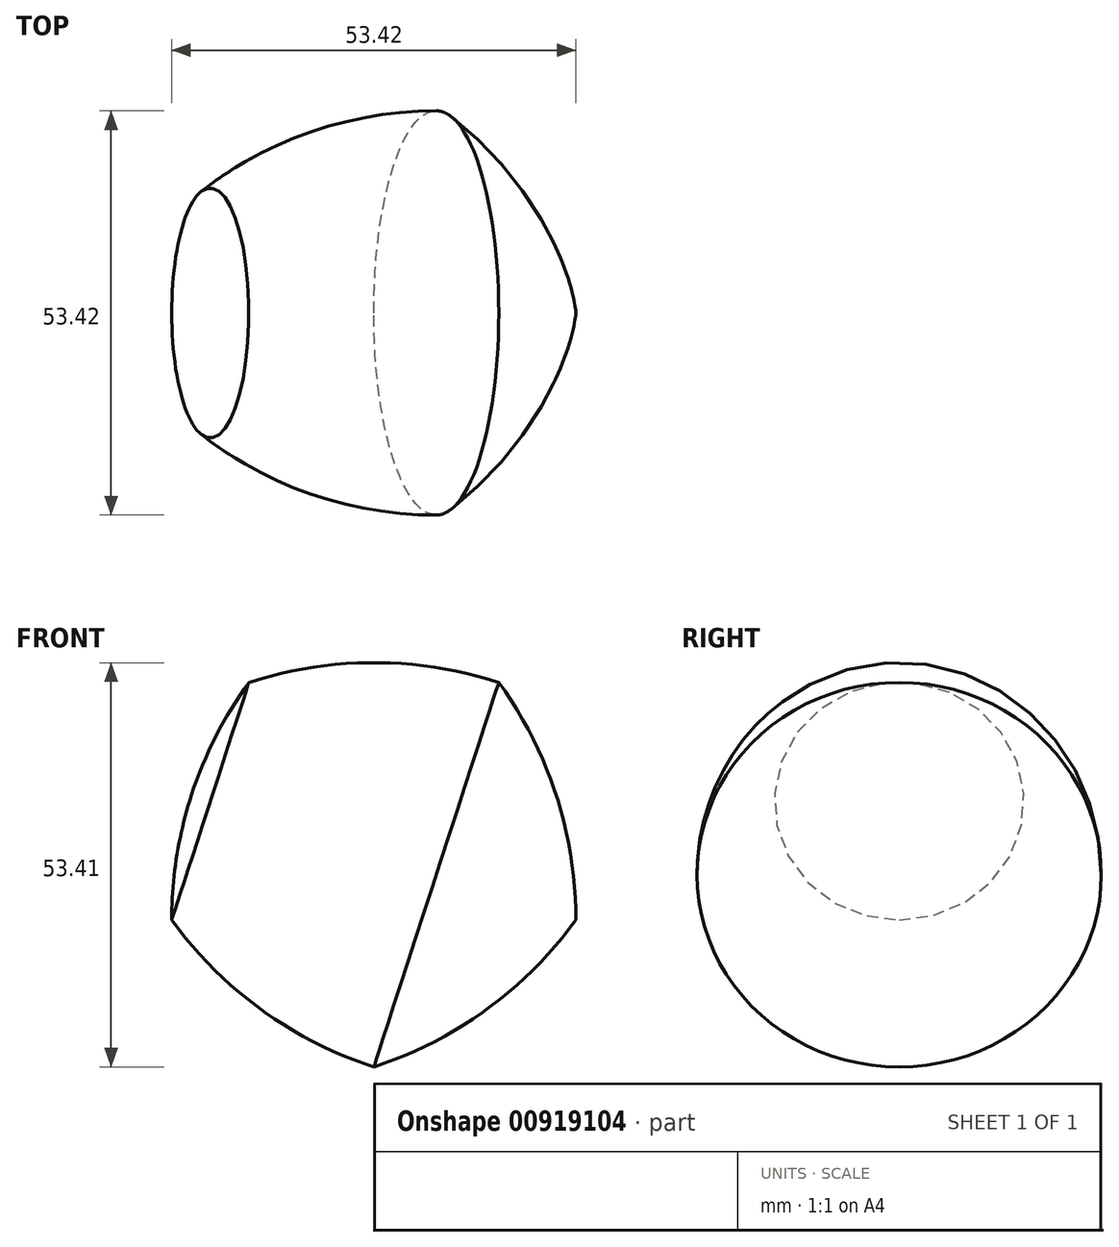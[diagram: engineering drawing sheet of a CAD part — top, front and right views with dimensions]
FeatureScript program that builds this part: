
annotation { "Feature Type Name" : "Feature", "Feature Type Description" : "" }
export const myFeature = defineFeature(function(context is Context, id is Id, definition is map)
    precondition{}
    {
        {
            var Q0;
            Q0=qCreatedBy(makeId("Front.planeOp"),FACE);
            var sketch = newSketch(context, id + "F0", { "sketchPlane" : qUnion([Q0])});
            skCircle(sketch, "E0.cCircle", {"center": v(0, 0) * mm, "radius": 22.72 * mm, "construction": true});
            skLineSegment(sketch, "E0.0", {"start": v(-16.5, 22.72) * mm, "end": v(16.5, 22.72) * mm});
            skLineSegment(sketch, "E0.1", {"start": v(16.5, 22.72) * mm, "end": v(26.7, -8.68) * mm});
            skLineSegment(sketch, "E0.2", {"start": v(26.7, -8.68) * mm, "end": v(0, -28.08) * mm});
            skLineSegment(sketch, "E0.3", {"start": v(0, -28.08) * mm, "end": v(-26.7, -8.68) * mm});
            skLineSegment(sketch, "E0.4", {"start": v(-26.7, -8.68) * mm, "end": v(-16.5, 22.72) * mm});
            skPoint(sketch, "E0.0.midPoint", {"position": v(0, 22.72) * mm});
            skPoint(sketch, "E1", {"position": v(-13.35, -18.38) * mm});
            skLineSegment(sketch, "E2", {"start": v(0, -28.08) * mm, "end": v(0, 22.72) * mm, "construction": true});
            skPoint(sketch, "E3", {"position": v(0, -22.72) * mm});
            skLineSegment(sketch, "E4", {"start": v(-21.6, 7.02) * mm, "end": v(26.7, -8.68) * mm});
            skArc(sketch, "E5", {"start": v(0, -28.08) * mm, "mid": v(14.9, -20.5) * mm, "end": v(26.7, -8.68) * mm});
            skArc(sketch, "E6", {"start": v(-26.7, -8.68) * mm, "mid": v(-14.9, -20.5) * mm, "end": v(0, -28.08) * mm});
            skArc(sketch, "E7.trimOffspring", {"start": v(16.5, 22.72) * mm, "mid": v(0, 25.33) * mm, "end": v(-16.5, 22.72) * mm});
            skArc(sketch, "E8.trimOffspring", {"start": v(-16.5, 22.72) * mm, "mid": v(-24.1, 7.83) * mm, "end": v(-26.7, -8.68) * mm});
            skArc(sketch, "E9.trimOffspring", {"start": v(26.7, -8.68) * mm, "mid": v(24.1, 7.83) * mm, "end": v(16.5, 22.72) * mm});
            skPoint(sketch, "E10", {"position": v(0, 25.33) * mm});
            skLineSegment(sketch, "E11", {"start": v(-21.6, 7.02) * mm, "end": v(-24.1, 7.83) * mm});
            skSolve(sketch);
        }
        {
            var Q0;
            {var subQ3=sQuery(id+"F0.wireOp",EDGE,"E11");Q0=makeQuery(id+"F0.imprint","IMPRINT",FACE,{"disambiguationData":[TD([[makeQuery(id+"F0.imprint","IMPRINT",EDGE,{"derivedFrom":subQ3}),1.0]])]});}
            var Q1;
            Q1=makeQuery(id+"F0.imprint","IMPRINT",FACE,{"disambiguationData":[TD([[makeQuery(id+"F0.imprint","IMPRINT",EDGE,{"derivedFrom":sQuery(id+"F0.wireOp",EDGE,"E0.2")}),-1.0]])]});
            var Q2;
            Q2=makeQuery(id+"F0.imprint","IMPRINT",FACE,{"disambiguationData":[TD([[makeQuery(id+"F0.imprint","IMPRINT",EDGE,{"derivedFrom":sQuery(id+"F0.wireOp",EDGE,"E0.3")}),1.0]])]});
            var Q3;
            Q3=makeQuery(id+"F0.imprint","IMPRINT",FACE,{"disambiguationData":[TD([[makeQuery(id+"F0.imprint","IMPRINT",EDGE,{"derivedFrom":sQuery(id+"F0.wireOp",EDGE,"E0.2")}),1.0]])]});
            var Q4;
            Q4=sQuery(id+"F0.wireOp",EDGE,"E11");
            revolve(context, id + "F1", {"surfaceOperationType" : NewSurfaceOperationType.NEW, "entities" : qUnion([Q0, Q1, Q2, Q3]), "axis" : qUnion([Q4]), "revolveType" : RevolveType.FULL});
        }
    });
